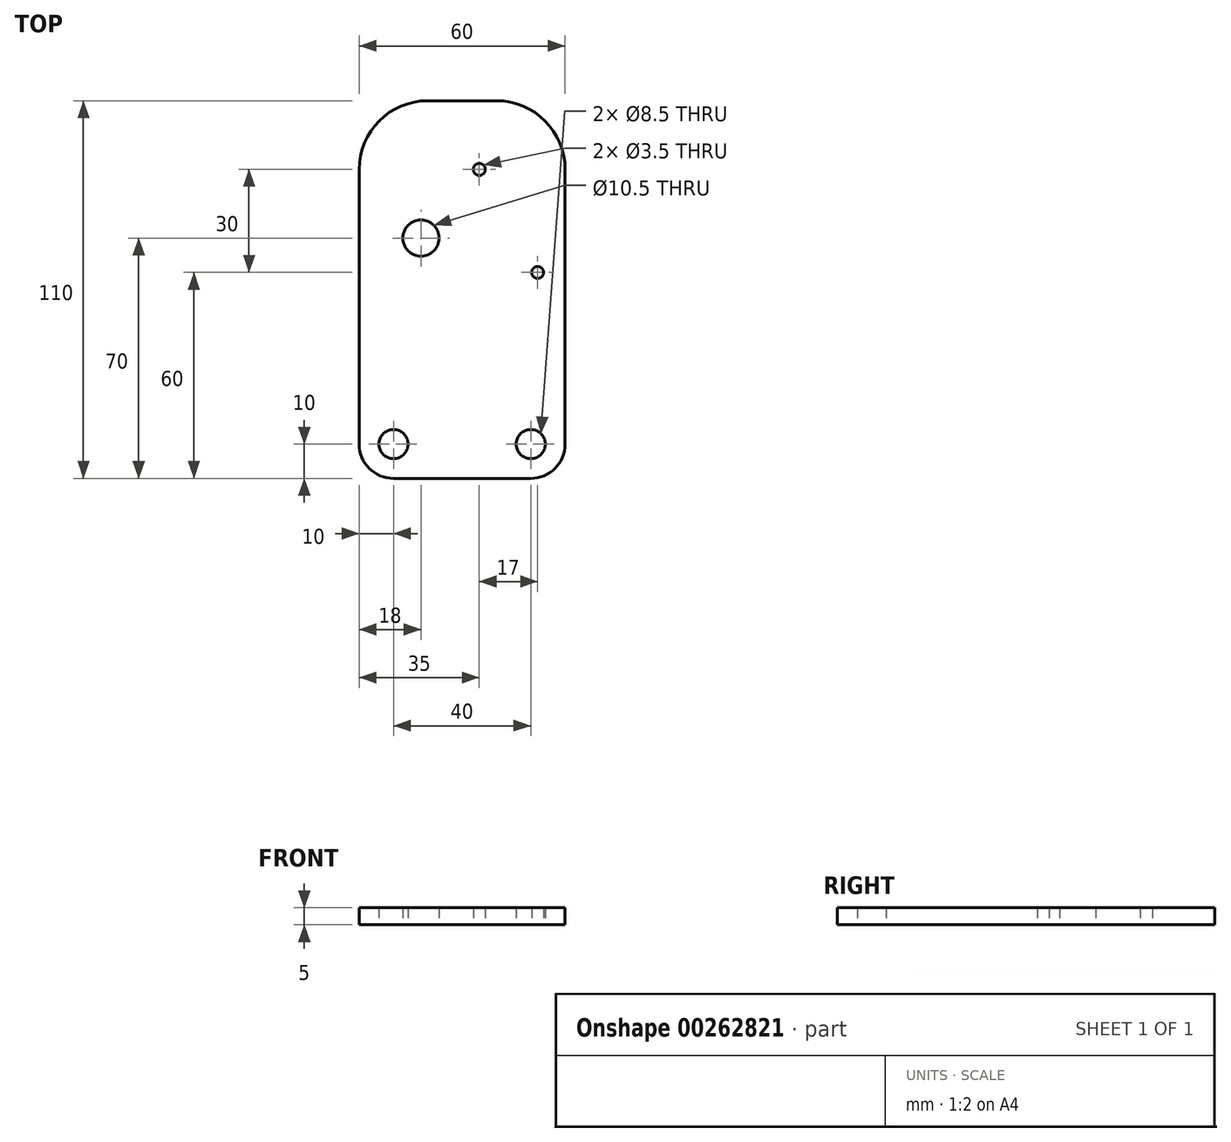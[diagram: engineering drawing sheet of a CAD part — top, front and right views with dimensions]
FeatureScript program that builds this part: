
annotation { "Feature Type Name" : "Feature", "Feature Type Description" : "" }
export const myFeature = defineFeature(function(context is Context, id is Id, definition is map)
    precondition{}
    {
        {
            var Q0;
            Q0=qCreatedBy(makeId("Top.planeOp"),FACE);
            var sketch = newSketch(context, id + "F0", { "sketchPlane" : qUnion([Q0])});
            skLineSegment(sketch, "E0.bottom", {"start": v(-30, 85) * mm, "end": v(30, 85) * mm});
            skLineSegment(sketch, "E0.top", {"start": v(-30, -25) * mm, "end": v(30, -25) * mm});
            skLineSegment(sketch, "E0.left", {"start": v(-30, 85) * mm, "end": v(-30, -25) * mm});
            skLineSegment(sketch, "E0.right", {"start": v(30, 85) * mm, "end": v(30, -25) * mm});
            skLineSegment(sketch, "E1", {"start": v(0, 0) * mm, "end": v(0, -25) * mm, "construction": true});
            skCircle(sketch, "E2", {"center": v(20, -15) * mm, "radius": 10 * mm, "construction": true});
            skCircle(sketch, "E3", {"center": v(-20, -15) * mm, "radius": 10 * mm, "construction": true});
            skLineSegment(sketch, "E4", {"start": v(-30, 45) * mm, "end": v(-12, 45) * mm, "construction": true});
            skLineSegment(sketch, "E5", {"start": v(22, 35) * mm, "end": v(22, 65) * mm, "construction": true});
            skLineSegment(sketch, "E6", {"start": v(22, 65) * mm, "end": v(5, 65) * mm, "construction": true});
            skSolve(sketch);
        }
        {
            var Q0;
            Q0 = qSketchRegion(id + "F0", true);
            extrude(context, id + "F1", {"entities" : qUnion([Q0]), "depth" : 5 * mm});
        }
        {
            var Q0;
            Q0=sQuery(id+"F0.wireOp",VERTEX,"E3.center");
            var Q1;
            Q1=sQuery(id+"F0.wireOp",VERTEX,"E2.center");
            var Q2;
            Q2=makeQuery(id+"F1.opExtrude","SWEPT_BODY",BODY,{"disambiguationData":[OSD([sQuery(id+"F0.wireOp",EDGE,"E0.bottom"),sQuery(id+"F0.wireOp",EDGE,"E0.top"),sQuery(id+"F0.wireOp",EDGE,"E0.left"),sQuery(id+"F0.wireOp",EDGE,"E0.right")])]});
            hole(context, id + "F2", {"style" : HoleStyle.SIMPLE, "endStyle" : HoleEndStyle.THROUGH, "oppositeDirection" : true, "holeDiameter" : 8.5 * mm, "tappedDepth" : 12 * mm, "tapClearance" : 3, "startFromSketch" : true, "locations" : qUnion([Q0, Q1]), "scope" : qUnion([Q2])});
        }
        {
            var Q0;
            Q0=sQuery(id+"F0.wireOp",VERTEX,"E4.end");
            var Q1;
            Q1=makeQuery(id+"F1.opExtrude","SWEPT_BODY",BODY,{"disambiguationData":[OSD([sQuery(id+"F0.wireOp",EDGE,"E0.bottom"),sQuery(id+"F0.wireOp",EDGE,"E0.top"),sQuery(id+"F0.wireOp",EDGE,"E0.left"),sQuery(id+"F0.wireOp",EDGE,"E0.right")])]});
            hole(context, id + "F3", {"style" : HoleStyle.SIMPLE, "endStyle" : HoleEndStyle.THROUGH, "oppositeDirection" : true, "holeDiameter" : 10.5 * mm, "tappedDepth" : 12 * mm, "tapClearance" : 3, "startFromSketch" : true, "locations" : qUnion([Q0]), "scope" : qUnion([Q1])});
        }
        {
            var Q0;
            Q0=sQuery(id+"F0.wireOp",VERTEX,"E6.end");
            var Q1;
            Q1=sQuery(id+"F0.wireOp",VERTEX,"E5.start");
            var Q2;
            Q2=makeQuery(id+"F1.opExtrude","SWEPT_BODY",BODY,{"disambiguationData":[OSD([sQuery(id+"F0.wireOp",EDGE,"E0.bottom"),sQuery(id+"F0.wireOp",EDGE,"E0.top"),sQuery(id+"F0.wireOp",EDGE,"E0.left"),sQuery(id+"F0.wireOp",EDGE,"E0.right")])]});
            hole(context, id + "F4", {"style" : HoleStyle.SIMPLE, "endStyle" : HoleEndStyle.THROUGH, "oppositeDirection" : true, "holeDiameter" : 3.5 * mm, "tappedDepth" : 12 * mm, "tapClearance" : 3, "startFromSketch" : true, "locations" : qUnion([Q0, Q1]), "scope" : qUnion([Q2])});
        }
        {
            var Q0;
            Q0=makeQuery(id+"F1.opExtrude","SWEPT_EDGE",EDGE,{"disambiguationData":[OSD([sQuery(id+"F0.wireOp",EDGE,"E0.top"),sQuery(id+"F0.wireOp",EDGE,"E0.left")])]});
            var Q1;
            Q1=makeQuery(id+"F1.opExtrude","SWEPT_EDGE",EDGE,{"disambiguationData":[OSD([sQuery(id+"F0.wireOp",EDGE,"E0.top"),sQuery(id+"F0.wireOp",EDGE,"E0.right")])]});
            fillet(context, id + "F5", {"entities" : qUnion([Q0, Q1]), "radius" : 10 * mm, "tangentPropagation" : true, "allowEdgeOverflow" : false});
        }
        {
            var Q0;
            Q0=makeQuery(id+"F1.opExtrude","SWEPT_EDGE",EDGE,{"disambiguationData":[OSD([sQuery(id+"F0.wireOp",EDGE,"E0.bottom"),sQuery(id+"F0.wireOp",EDGE,"E0.left")])]});
            var Q1;
            Q1=makeQuery(id+"F1.opExtrude","SWEPT_EDGE",EDGE,{"disambiguationData":[OSD([sQuery(id+"F0.wireOp",EDGE,"E0.bottom"),sQuery(id+"F0.wireOp",EDGE,"E0.right")])]});
            fillet(context, id + "F6", {"entities" : qUnion([Q0, Q1]), "radius" : 20 * mm, "tangentPropagation" : true, "allowEdgeOverflow" : false});
        }
    });
